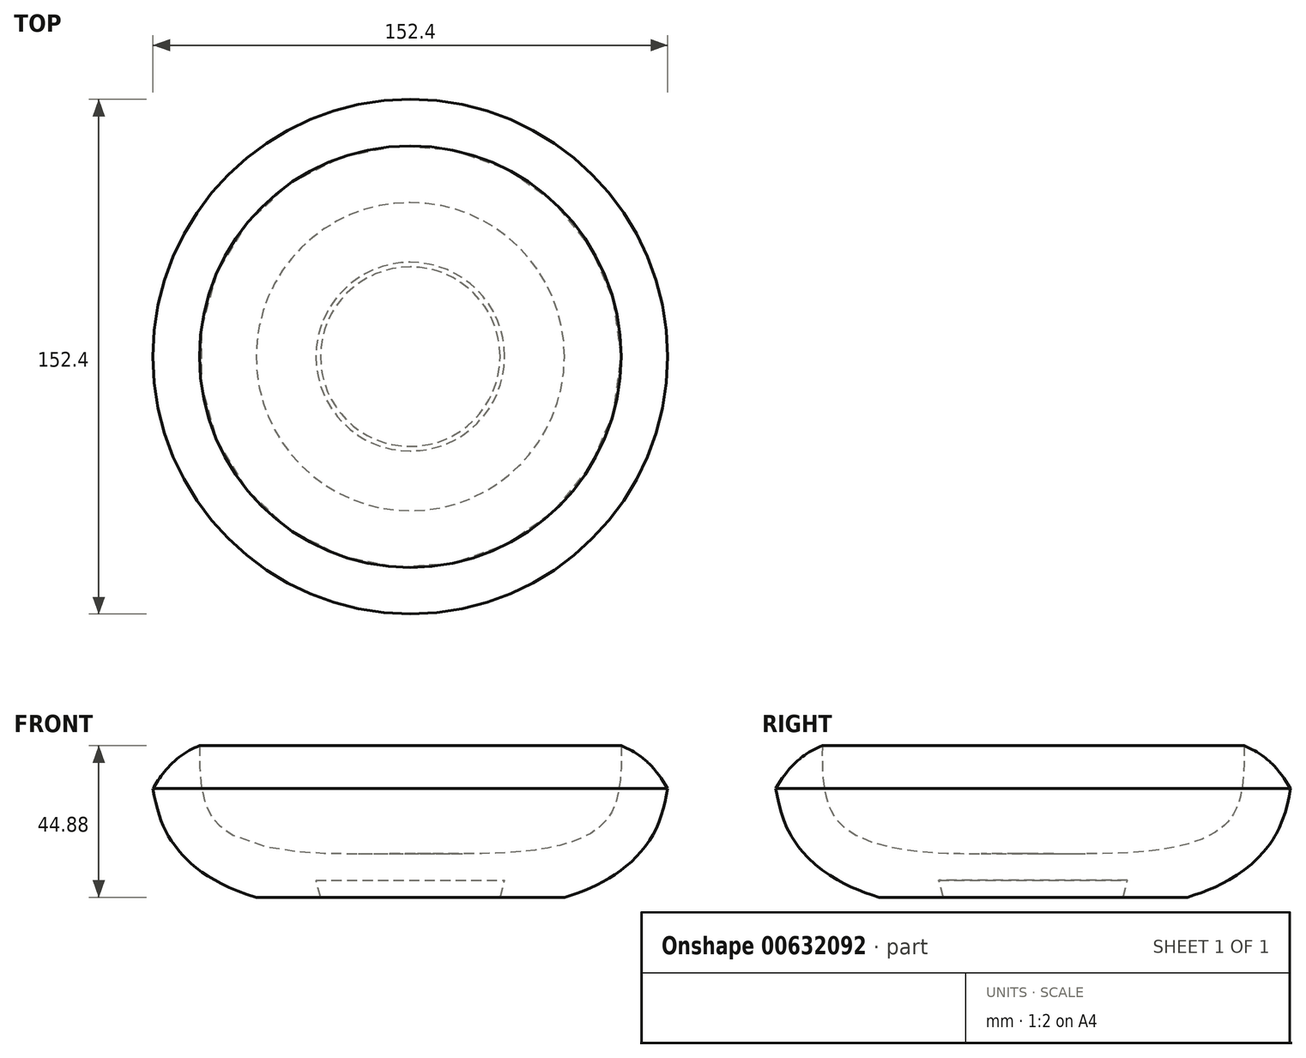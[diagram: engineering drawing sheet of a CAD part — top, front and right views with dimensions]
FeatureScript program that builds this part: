
annotation { "Feature Type Name" : "Feature", "Feature Type Description" : "" }
export const myFeature = defineFeature(function(context is Context, id is Id, definition is map)
    precondition{}
    {
        {
            var Q0;
            Q0=qCreatedBy(makeId("Front.planeOp"),FACE);
            var sketch = newSketch(context, id + "F0", { "sketchPlane" : qUnion([Q0])});
            skLineSegment(sketch, "E0.bottom", {"start": v(0, 0) * mm, "end": v(76.2, 0) * mm, "construction": true});
            skLineSegment(sketch, "E0.top", {"start": v(0, 50.8) * mm, "end": v(76.2, 50.8) * mm, "construction": true});
            skLineSegment(sketch, "E0.left", {"start": v(0, 0) * mm, "end": v(0, 50.8) * mm, "construction": true});
            skLineSegment(sketch, "E0.right", {"start": v(76.2, 0) * mm, "end": v(76.2, 50.8) * mm, "construction": true});
            skLineSegment(sketch, "E1", {"start": v(0, 5.08) * mm, "end": v(27.94, 5.08) * mm});
            skLineSegment(sketch, "E2", {"start": v(27.94, 5.08) * mm, "end": v(26.58, 0) * mm});
            skLineSegment(sketch, "E3", {"start": v(26.58, 0) * mm, "end": v(45.63, 0) * mm});
            skFitSpline(sketch, "E4", {"points": [v(76.2, 32.22) * mm, v(69.52, 15) * mm, v(45.63, 0) * mm], "startDerivative": vector(-8.84, -52.02) * mm, "endDerivative": vector(-67.48, -19.96) * mm});
            skFitSpline(sketch, "E5", {"points": [v(76.2, 32.22) * mm, v(71.15, 39.07) * mm, v(62.43, 44.88) * mm], "startDerivative": vector(-7.55, 12.27) * mm, "endDerivative": vector(-17.57, 6.41) * mm});
            skFitSpline(sketch, "E6", {"points": [v(62.43, 44.88) * mm, v(60.33, 26.68) * mm, v(49.87, 17.15) * mm, v(28.35, 13.2) * mm, v(0, 12.91) * mm], "startDerivative": vector(1.08, -68.23) * mm, "endDerivative": vector(-100.96, -1.46) * mm});
            skLineSegment(sketch, "E7", {"start": v(0, 12.91) * mm, "end": v(0, 5.08) * mm});
            skSolve(sketch);
        }
        {
            var Q0;
            Q0=qSketchRegion(id+"F0",true);
            var Q1;
            Q1=sQuery(id+"F0.wireOp",EDGE,"E0.left");
            revolve(context, id + "F1", {"entities" : qUnion([Q0]), "axis" : qUnion([Q1]), "revolveType" : RevolveType.FULL});
        }
    });
